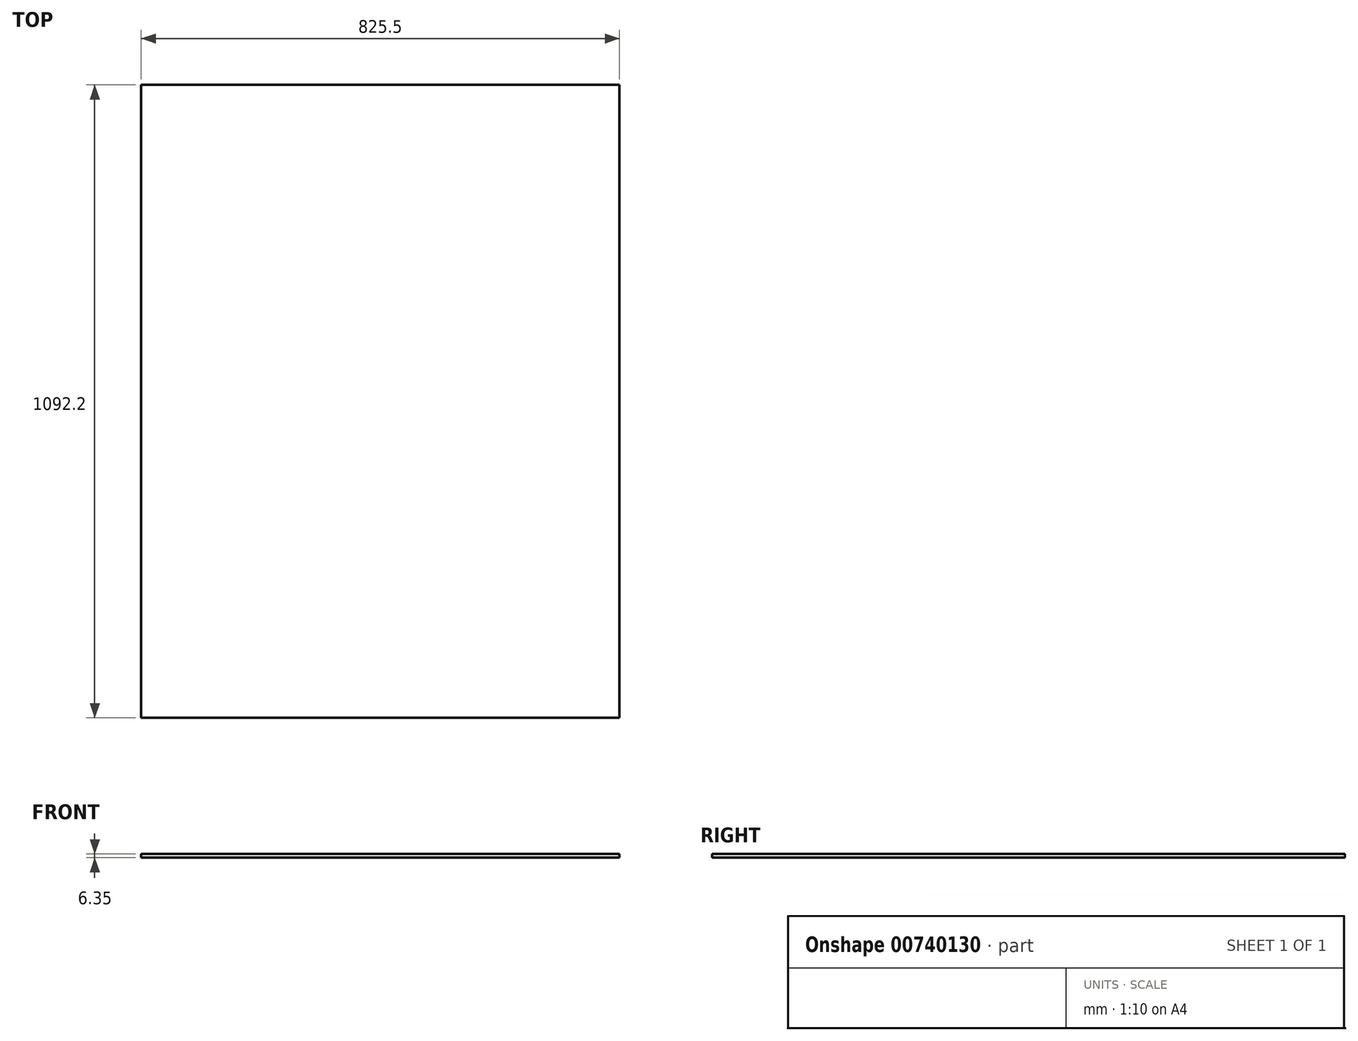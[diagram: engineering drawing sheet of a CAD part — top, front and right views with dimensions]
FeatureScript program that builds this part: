
annotation { "Feature Type Name" : "Feature", "Feature Type Description" : "" }
export const myFeature = defineFeature(function(context is Context, id is Id, definition is map)
    precondition{}
    {
        {
            var Q0;
            Q0=qCreatedBy(makeId("Top.planeOp"),FACE);
            var sketch = newSketch(context, id + "F0", { "sketchPlane" : qUnion([Q0])});
            skLineSegment(sketch, "E0.bottom", {"start": v(847.8, -203.66) * mm, "end": v(22.3, -203.66) * mm});
            skLineSegment(sketch, "E0.top", {"start": v(847.8, 888.54) * mm, "end": v(22.3, 888.54) * mm});
            skLineSegment(sketch, "E0.left", {"start": v(847.8, -203.66) * mm, "end": v(847.8, 888.54) * mm});
            skLineSegment(sketch, "E0.right", {"start": v(22.3, -203.66) * mm, "end": v(22.3, 888.54) * mm});
            skSolve(sketch);
        }
        {
            var Q0;
            Q0=makeQuery(id+"F0.imprint","IMPRINT",FACE,{"disambiguationData":[TD([[makeQuery(id+"F0.imprint","IMPRINT",EDGE,{"derivedFrom":sQuery(id+"F0.wireOp",EDGE,"E0.right")}),1.0]])]});
            var Q1;
            Q1=makeQuery(id+"F0.imprint","IMPRINT",FACE,{"disambiguationData":[TD([[makeQuery(id+"F0.imprint","IMPRINT",EDGE,{"derivedFrom":sQuery(id+"F0.wireOp",EDGE,"E0.bottom")}),-1.0]])]});
            extrude(context, id + "F1", {"entities" : qUnion([Q0, Q1]), "depth" : 6.35 * mm, "offsetDistance" : 25.4 * mm});
        }
    });
